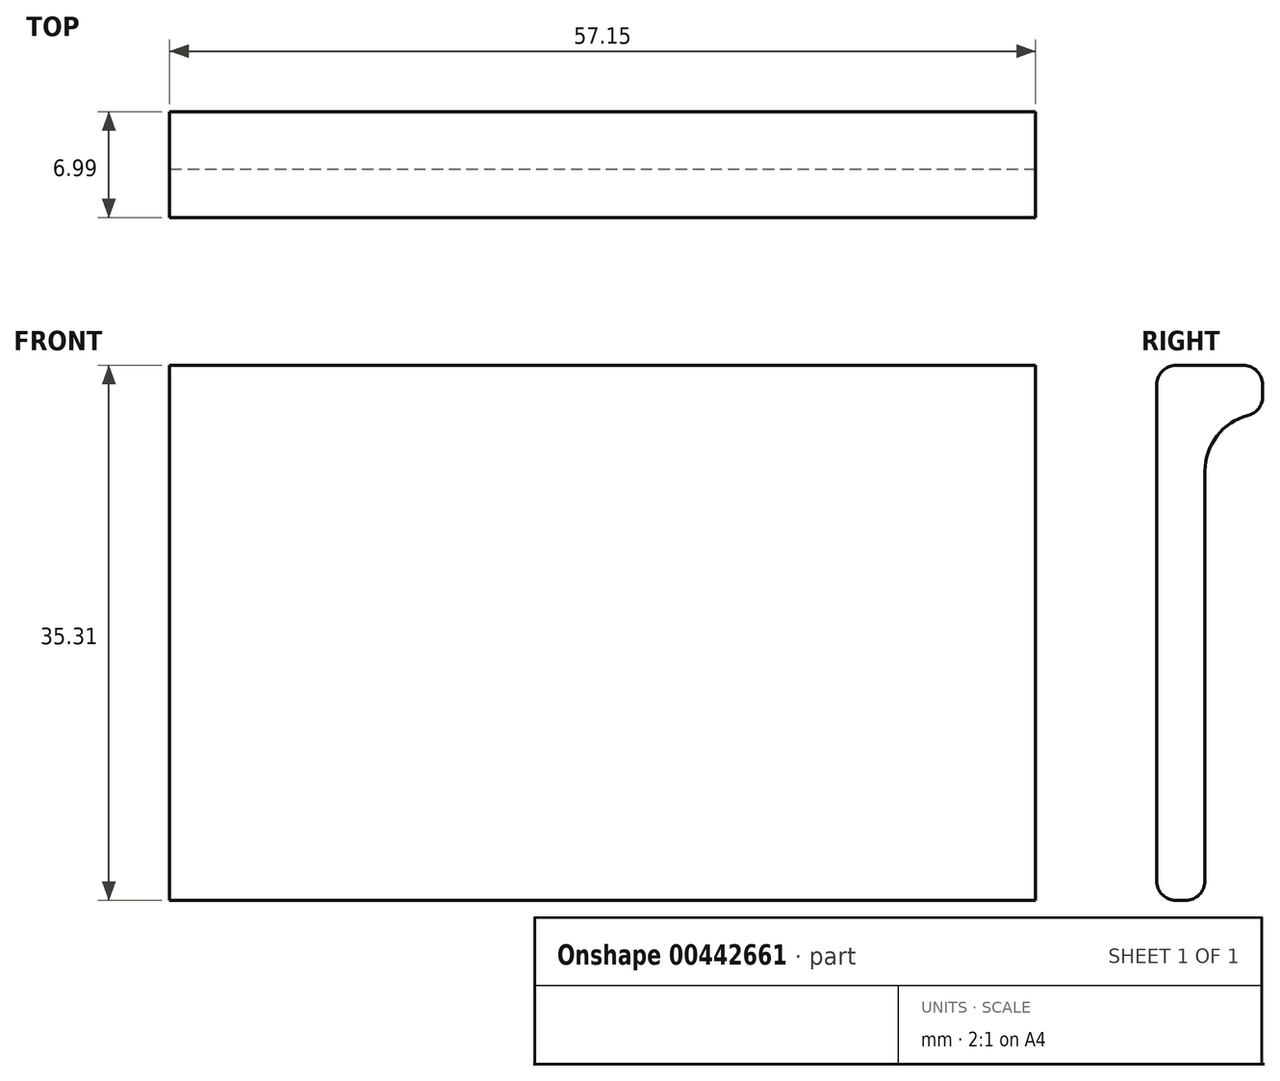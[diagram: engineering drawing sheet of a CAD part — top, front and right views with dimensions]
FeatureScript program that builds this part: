
annotation { "Feature Type Name" : "Feature", "Feature Type Description" : "" }
export const myFeature = defineFeature(function(context is Context, id is Id, definition is map)
    precondition{}
    {
        {
            var Q0;
            Q0=qCreatedBy(makeId("Right.planeOp"),FACE);
            var sketch = newSketch(context, id + "F0", { "sketchPlane" : qUnion([Q0])});
            skLineSegment(sketch, "E0", {"start": v(0, 1.27) * mm, "end": v(0, 28.96) * mm});
            skLineSegment(sketch, "E1", {"start": v(1.27, 0) * mm, "end": v(1.9, 0) * mm});
            skLineSegment(sketch, "E2", {"start": v(6.99, 34.04) * mm, "end": v(6.99, 33.24) * mm});
            skLineSegment(sketch, "E3", {"start": v(0, 28.96) * mm, "end": v(0, 34.04) * mm});
            skPoint(sketch, "E4.orphan", {"position": v(8.34, 32.13) * mm});
            skPoint(sketch, "E5.orphan", {"position": v(3.05, 28.96) * mm});
            skLineSegment(sketch, "E6", {"start": v(3.18, 1.27) * mm, "end": v(3.18, 28.32) * mm});
            skPoint(sketch, "E7.end.orphan", {"position": v(2.36, 32.13) * mm});
            skLineSegment(sketch, "E8", {"start": v(6.99, 32.13) * mm, "end": v(6.99, 32.13) * mm});
            skLineSegment(sketch, "E9", {"start": v(1.27, 35.3) * mm, "end": v(5.72, 35.3) * mm});
            skPoint(sketch, "E10.visualSharp", {"position": v(3.18, 32.13) * mm});
            skArc(sketch, "E10.filletArc", {"start": v(6.03, 32.01) * mm, "mid": v(3.97, 30.65) * mm, "end": v(3.18, 28.32) * mm});
            skPoint(sketch, "E11.visualSharp", {"position": v(6.99, 35.3) * mm});
            skArc(sketch, "E11.filletArc", {"start": v(6.99, 34.04) * mm, "mid": v(6.61, 34.93) * mm, "end": v(5.72, 35.3) * mm});
            skPoint(sketch, "E12.visualSharp", {"position": v(0, 35.3) * mm});
            skArc(sketch, "E12.filletArc", {"start": v(1.27, 35.3) * mm, "mid": v(0.37, 34.93) * mm, "end": v(0, 34.04) * mm});
            skPoint(sketch, "E13.visualSharp", {"position": v(3.18, 0) * mm});
            skArc(sketch, "E13.filletArc", {"start": v(1.9, 0) * mm, "mid": v(2.8, 0.37) * mm, "end": v(3.17, 1.27) * mm});
            skPoint(sketch, "E14.visualSharp", {"position": v(0, 0) * mm});
            skArc(sketch, "E14.filletArc", {"start": v(0, 1.27) * mm, "mid": v(0.37, 0.37) * mm, "end": v(1.27, 0) * mm});
            skPoint(sketch, "E15.visualSharp", {"position": v(6.99, 32.13) * mm});
            skArc(sketch, "E15.filletArc", {"start": v(6.03, 32.01) * mm, "mid": v(6.72, 32.46) * mm, "end": v(6.99, 33.24) * mm});
            skSolve(sketch);
        }
        {
            var Q0;
            Q0=makeQuery(id+"F0.imprint","IMPRINT",FACE,{"disambiguationData":[TD([[makeQuery(id+"F0.imprint","IMPRINT",EDGE,{"derivedFrom":sQuery(id+"F0.wireOp",EDGE,"E0")}),-1.0]])]});
            extrude(context, id + "F1", {"entities" : qUnion([Q0]), "depth" : 57.15 * mm});
        }
    });
